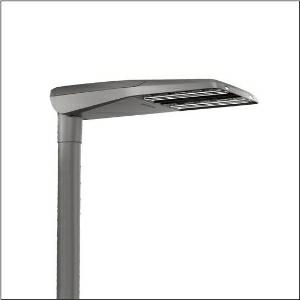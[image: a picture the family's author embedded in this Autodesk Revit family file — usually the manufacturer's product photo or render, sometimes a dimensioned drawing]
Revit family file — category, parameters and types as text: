
# Revit family: streetlight_sl_11_iq_midi___st1_2a_5xc3a51f08le_94b4
name_source: partatom
category: Lighting Fixtures
units: mm (PartAtom-declared; Revit-internal decimal feet)

## family parameters
Cut with Voids When Loaded = No
Host = Face
Light Source = No
Part Type = Normal
Room Calculation Point = No
Round Connector Dimension = Use Diameter
Shared = No

## types (1)
- --- (1 x LED, 9210 lm, 60.4 W, 3000K)
    Apparent Load = 60 VA
    CIE Flux Codes = 32 70 96 100 100
    Color Rendering = 70
    Color Temperature = 3000K
    Default Elevation = 1800 mm
    Description = Streetlight SL 11 iQ midi, mast luminaire, primary light control with 3 zone facetted reflector, of plastic, silver coated, highly specular, primary optical cover: cover, of PMMA, transparent, light distribution: ST1.2a, light emission: direct distribution, primary light characteristic: asymmetric, installation type: post-top, side-entry, lamps: LED, High Power LED, rated values: 9.210lm | 60,4W | 152,5lm/W (begin service life); end service life: 9.210lm | 62,5W; at 50% lumin. flux: 4.605lm | 29,6W | 155,6lm/W, colour temperature: 3000K, colour rendering: CRI > 70, light colour: 730, light setting 1 begin service life: 100% | 9.210lm | 60,4W | 152,5lm/W | 3.000K, light setting 1 end service life: 62,5W, further light settings possible, control: Street-Remote, optimised constant luminous flux control (CLO 2.0), Desk-Remote (wireless, voltage-free reading and setting of iQ features in the workshop via application-optimized NFC function/RFID function), Light-Fading, Smart-Wire, Night-Set, Lumen-Switch, Temp-Guard, Auto-Match, with cable H07RN-F 3x 1.5mm², mains connection: 230..240V, AC, 50/60Hz, connection cable pre-assembled, cable length: 8,5m, luminaire housing, of diecast aluminium, powder-coated, SITECO metallic grey (DB 702S), please order mast flange separately, inclination adjustable without tools: 0°, 5°, 10°, 15° (post-top) | 0°, -5°, -10°, -15° (side-entry), sealing non-destructively replaceable, multi-level sealing system, length: 780mm, width: 376mm, height: 118mm, mast flange for spigot size: 42mm (side-entry): 5XC10008XM4, 60/48mm (side-entry/post-top): 5XC10108XM2, 76/60mm (side-entry/post-top): 5XC10108XM1, equipment: standard, protection rating (complete): IP66, insulation class (complete): insulation class II (safety insulation), certification: CE, ENEC, ENEC+, VDE, impact resistance: IK10, permissible operating ambient temperature for outdoor applications: -25..+50°C, standard-compliant lighting for roads and squares, Environmental Product Declaration (EPD) tested and certified by an independent institute, packaging unit: 1 piece

Light Distribution: ST1.2a
    Height = 118 mm
    Lamp = 1 x LED
    Lamp Light Flux = 9210 lm
    Lamp Power = 60.4 W
    Lamp count = 1
    Length = 780 mm
    Luminous efficacy = 152 lm/W
    Manufacturer = Siteco
    ModVariant = No
    Model = 5XC3A51F08LE
    Number of Poles = 1
    OnlyDefault = Yes
    Power Factor = 1
    Product Name = Streetlight SL 11 iQ midi | ST1.2a
    Product group = mast luminaire | pylon top
    ProductGroupID = 6100
    Protection Class = Protection class II
    Protection Degree = IP 66
    RLX_Detail_Level = 1
    RLX_Emergency_Light_Flux = 0 lm
    RLX_Emergency_Type = 0
    RLX_Emergency_Type_DB = No
    RlxData = <blob elided: 70821 chars, md5=06a4b13a>
    Socket = socket
    Standby Power = 0 W
    System Light Flux = 9210 lm
    System Power = 60 W
    Type Comments = factory setting: luminous flux: 100 % | dim-lin: 254 | 520 mA
    Type Image = l_1005960.jpg
    URL = http://relux.com
    VarID = @adj_194407
    Voltage = 0 V
    Weight = 0.00 kg
    Width = 376 mm

## geometry (parser evidence)
native form markers: Blend x4, Sweep x9
no freeform markers — native parametric forms only
